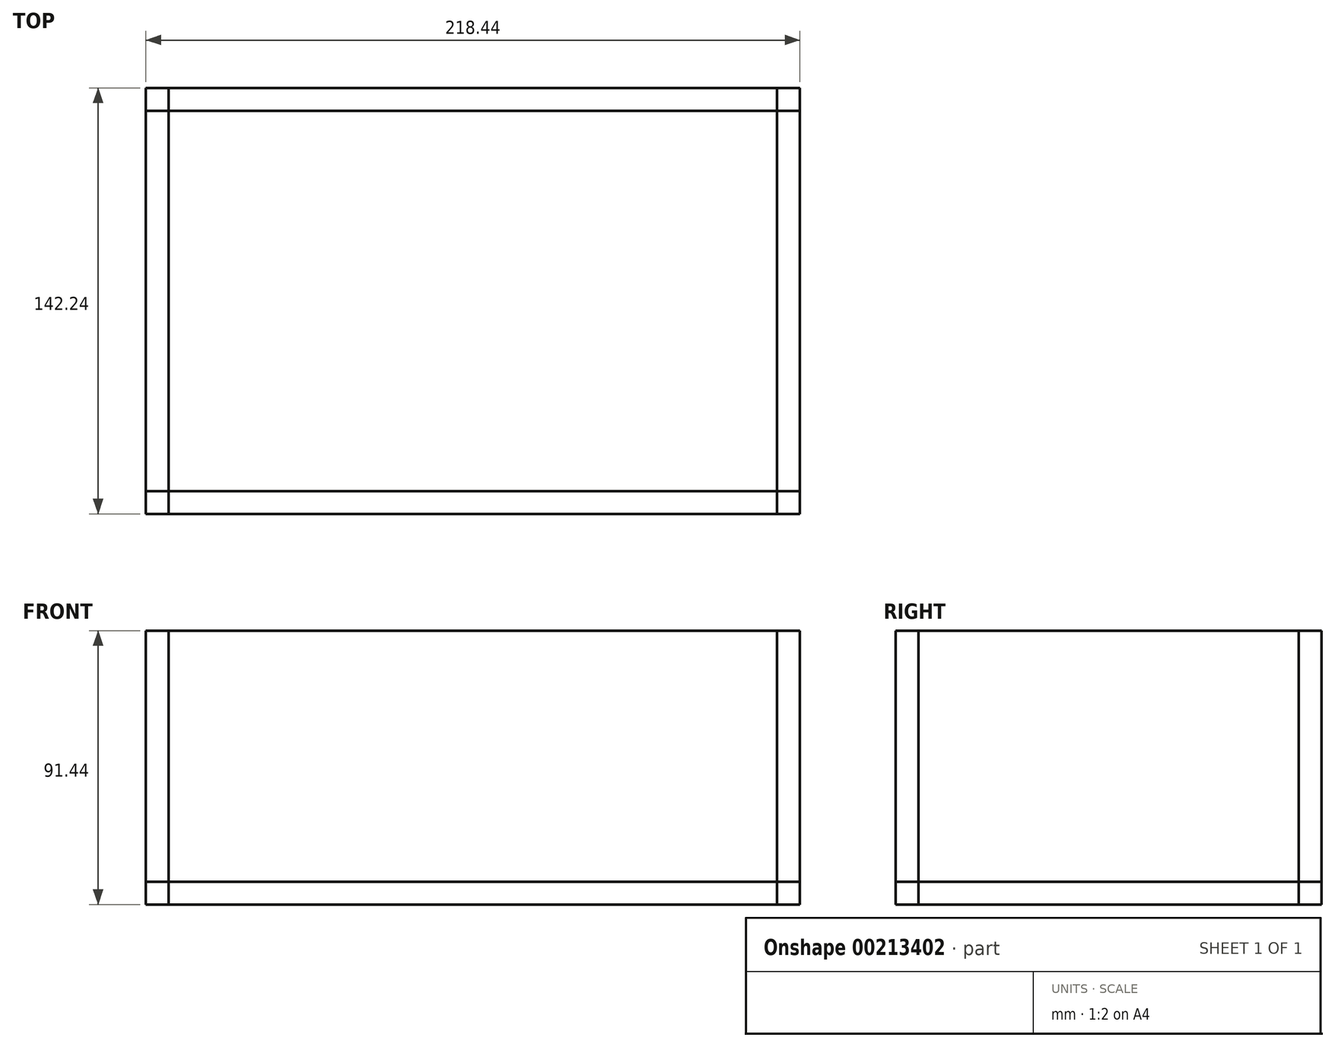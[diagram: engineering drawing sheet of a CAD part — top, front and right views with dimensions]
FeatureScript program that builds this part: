
annotation { "Feature Type Name" : "Feature", "Feature Type Description" : "" }
export const myFeature = defineFeature(function(context is Context, id is Id, definition is map)
    precondition{}
    {
        {
            var Q0;
            Q0=qCreatedBy(makeId("Top.planeOp"),FACE);
            var sketch = newSketch(context, id + "F0", { "sketchPlane" : qUnion([Q0])});
            skLineSegment(sketch, "E0.bottom", {"start": v(-109.22, 71.12) * mm, "end": v(109.22, 71.12) * mm});
            skLineSegment(sketch, "E0.top", {"start": v(-109.22, -71.12) * mm, "end": v(109.22, -71.12) * mm});
            skLineSegment(sketch, "E0.left", {"start": v(-109.22, 71.12) * mm, "end": v(-109.22, -71.12) * mm});
            skLineSegment(sketch, "E0.right", {"start": v(109.22, 71.12) * mm, "end": v(109.22, -71.12) * mm});
            skPoint(sketch, "E0.middle", {"position": v(0, 0) * mm});
            skSolve(sketch);
        }
        {
            var Q0;
            Q0=makeQuery(id+"F0.imprint","IMPRINT",FACE,{"disambiguationData":[TD([[makeQuery(id+"F0.imprint","IMPRINT",EDGE,{"derivedFrom":sQuery(id+"F0.wireOp",EDGE,"E0.bottom")}),-1.0]])]});
            extrude(context, id + "F1", {"entities" : qUnion([Q0]), "depth" : 7.62 * mm});
        }
        {
            var Q0;
            Q0=qCreatedBy(makeId("Front.planeOp"),FACE);
            cPlane(context, id + "F2", {"entities" : qUnion([Q0]), "cplaneType" : CPlaneType.OFFSET, "offset" : 71.12 * mm, "width" : 152.4 * mm, "height" : 152.4 * mm});
        }
        {
            var Q0;
            Q0=qCreatedBy(id+"F2.planeOp",FACE);
            var sketch = newSketch(context, id + "F3", { "sketchPlane" : qUnion([Q0])});
            skLineSegment(sketch, "E1", {"start": v(0, 0) * mm, "end": v(109.22, 0) * mm});
            skLineSegment(sketch, "E2.MirrorCS", {"start": v(0, 0) * mm, "end": v(-109.22, 0) * mm});
            skLineSegment(sketch, "E3", {"start": v(-109.22, 0) * mm, "end": v(-109.22, 91.44) * mm});
            skLineSegment(sketch, "E4.MirrorCS", {"start": v(109.22, 0) * mm, "end": v(109.22, 91.44) * mm});
            skLineSegment(sketch, "E5", {"start": v(-109.22, 91.44) * mm, "end": v(109.22, 91.44) * mm});
            skSolve(sketch);
        }
        {
            var Q0;
            Q0=makeQuery(id+"F3.imprint","IMPRINT",FACE,{"disambiguationData":[TD([[makeQuery(id+"F3.imprint","IMPRINT",EDGE,{"derivedFrom":sQuery(id+"F3.wireOp",EDGE,"E1")}),1.0]])]});
            extrude(context, id + "F4", {"entities" : qUnion([Q0]), "oppositeDirection" : true, "depth" : 7.62 * mm});
        }
        {
            var Q0;
            Q0=makeQuery(id+"F4.opExtrude","SWEPT_BODY",BODY,{"disambiguationData":[OSD([sQuery(id+"F3.wireOp",EDGE,"E1"),sQuery(id+"F3.wireOp",EDGE,"E2.MirrorCS"),sQuery(id+"F3.wireOp",EDGE,"E3"),sQuery(id+"F3.wireOp",EDGE,"E4.MirrorCS"),sQuery(id+"F3.wireOp",EDGE,"E5")])]});
            var Q1;
            Q1=qCreatedBy(makeId("Front.planeOp"),FACE);
            mirror(context, id + "F5", {"entities" : qUnion([Q0]), "mirrorPlane" : qUnion([Q1])});
        }
        {
            var Q0;
            Q0=qCreatedBy(makeId("Right.planeOp"),FACE);
            cPlane(context, id + "F6", {"entities" : qUnion([Q0]), "cplaneType" : CPlaneType.OFFSET, "offset" : 109.22 * mm, "width" : 152.4 * mm, "height" : 152.4 * mm});
        }
        {
            var Q0;
            Q0=qCreatedBy(id+"F6.planeOp",FACE);
            var sketch = newSketch(context, id + "F7", { "sketchPlane" : qUnion([Q0])});
            skLineSegment(sketch, "E6", {"start": v(0, 0) * mm, "end": v(-71.12, 0) * mm});
            skLineSegment(sketch, "E7", {"start": v(-71.12, 0) * mm, "end": v(-71.12, 91.44) * mm});
            skLineSegment(sketch, "E8.MirrorCS", {"start": v(0, 0) * mm, "end": v(71.12, 0) * mm});
            skLineSegment(sketch, "E9.MirrorCS", {"start": v(71.12, 0) * mm, "end": v(71.12, 91.44) * mm});
            skLineSegment(sketch, "E10", {"start": v(-71.12, 91.44) * mm, "end": v(71.12, 91.44) * mm});
            skSolve(sketch);
        }
        {
            var Q0;
            Q0=makeQuery(id+"F7.imprint","IMPRINT",FACE,{"disambiguationData":[TD([[makeQuery(id+"F7.imprint","IMPRINT",EDGE,{"derivedFrom":sQuery(id+"F7.wireOp",EDGE,"E6")}),-1.0]])]});
            extrude(context, id + "F8", {"entities" : qUnion([Q0]), "oppositeDirection" : true, "depth" : 7.62 * mm});
        }
        {
            var Q0;
            Q0=makeQuery(id+"F8.opExtrude","SWEPT_BODY",BODY,{"disambiguationData":[OSD([sQuery(id+"F7.wireOp",EDGE,"E6"),sQuery(id+"F7.wireOp",EDGE,"E7"),sQuery(id+"F7.wireOp",EDGE,"E8.MirrorCS"),sQuery(id+"F7.wireOp",EDGE,"E9.MirrorCS"),sQuery(id+"F7.wireOp",EDGE,"E10")])]});
            var Q1;
            Q1=qCreatedBy(makeId("Right.planeOp"),FACE);
            mirror(context, id + "F9", {"entities" : qUnion([Q0]), "mirrorPlane" : qUnion([Q1])});
        }
    });
